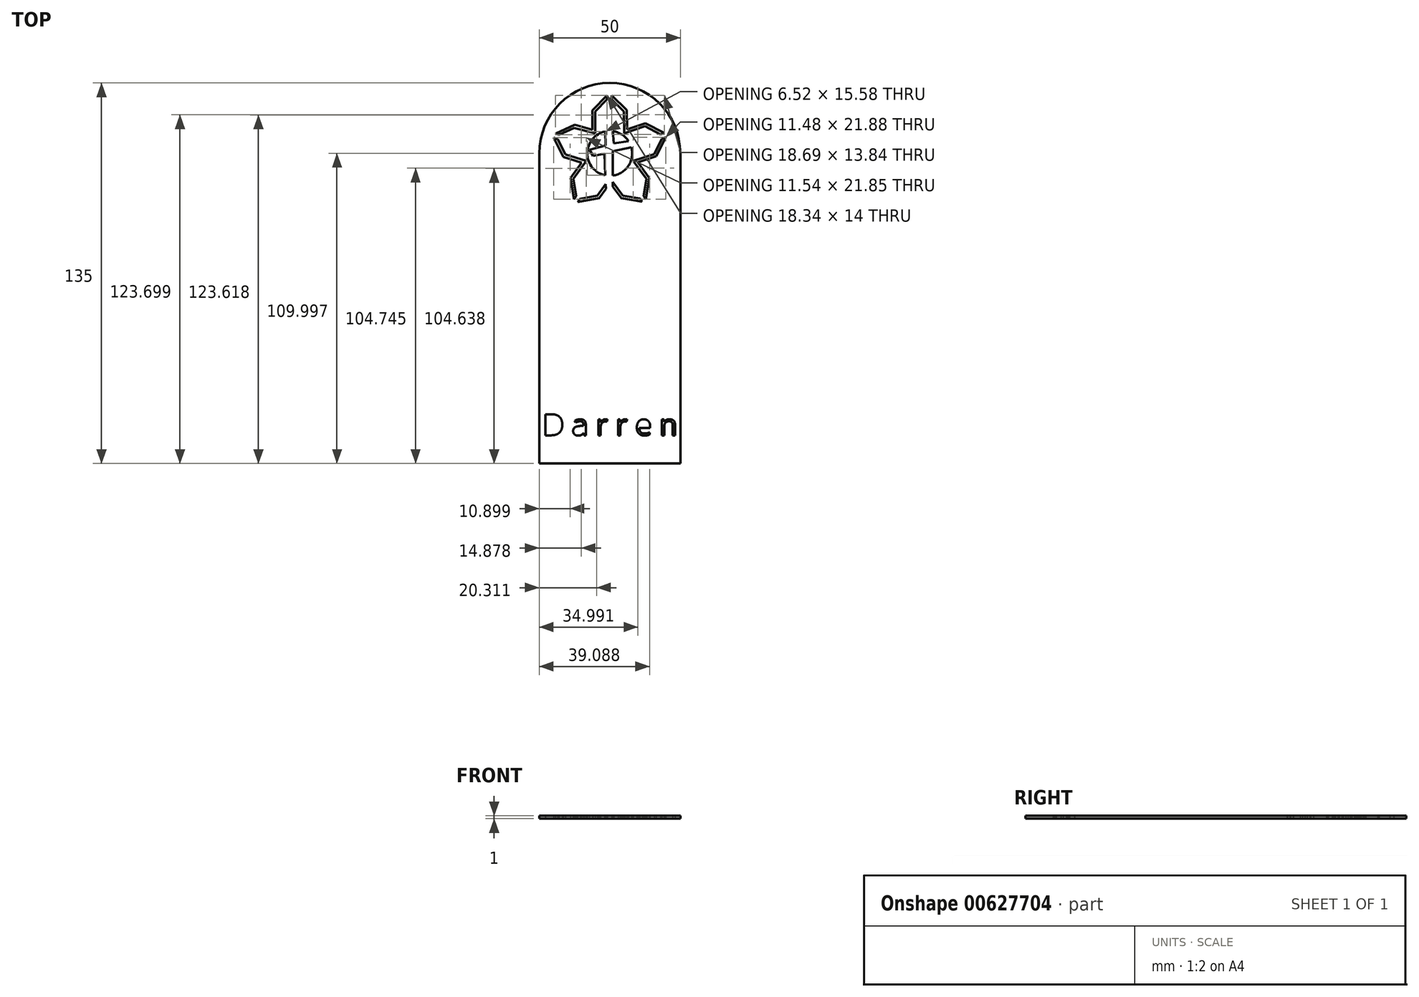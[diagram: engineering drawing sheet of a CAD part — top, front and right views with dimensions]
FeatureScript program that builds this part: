
annotation { "Feature Type Name" : "Feature", "Feature Type Description" : "" }
export const myFeature = defineFeature(function(context is Context, id is Id, definition is map)
    precondition{}
    {
        {
            var Q0;
            Q0=qCreatedBy(makeId("Top.planeOp"),FACE);
            var sketch = newSketch(context, id + "F0", { "sketchPlane" : qUnion([Q0])});
            skArc(sketch, "E0", {"start": v(1.43, 12.5) * mm, "mid": v(-23.57, 37.5) * mm, "end": v(-48.57, 12.5) * mm});
            skLineSegment(sketch, "E1", {"start": v(-28.74, 19.57) * mm, "end": v(-28.74, 27.36) * mm});
            skLineSegment(sketch, "E2", {"start": v(-28.74, 27.36) * mm, "end": v(-24.52, 31.68) * mm});
            skLineSegment(sketch, "E3", {"start": v(-22.92, 31.71) * mm, "end": v(-18.59, 27.41) * mm});
            skLineSegment(sketch, "E4", {"start": v(-18.59, 27.41) * mm, "end": v(-18.45, 19.6) * mm});
            skLineSegment(sketch, "E5", {"start": v(-18.45, 19.6) * mm, "end": v(-11.04, 22.13) * mm});
            skLineSegment(sketch, "E6", {"start": v(-11.04, 22.13) * mm, "end": v(-5.57, 19.28) * mm});
            skLineSegment(sketch, "E7", {"start": v(-5.08, 17.75) * mm, "end": v(-7.83, 12.32) * mm});
            skLineSegment(sketch, "E8", {"start": v(-7.83, 12.32) * mm, "end": v(-15.22, 9.9) * mm});
            skLineSegment(sketch, "E9", {"start": v(-15.22, 9.9) * mm, "end": v(-10.56, 3.45) * mm});
            skLineSegment(sketch, "E10", {"start": v(-10.56, 3.45) * mm, "end": v(-11.6, -2.55) * mm});
            skLineSegment(sketch, "E11", {"start": v(-12.9, -3.48) * mm, "end": v(-18.94, -2.5) * mm});
            skLineSegment(sketch, "E12", {"start": v(-18.94, -2.5) * mm, "end": v(-22.48, 2.4) * mm});
            skLineSegment(sketch, "E13", {"start": v(-27.97, -2.5) * mm, "end": v(-34.11, -3.56) * mm});
            skLineSegment(sketch, "E14", {"start": v(-35.42, -2.63) * mm, "end": v(-36.47, 3.45) * mm});
            skLineSegment(sketch, "E15", {"start": v(-36.47, 3.45) * mm, "end": v(-31.9, 9.82) * mm});
            skLineSegment(sketch, "E16", {"start": v(-31.9, 9.82) * mm, "end": v(-39.32, 12.08) * mm});
            skLineSegment(sketch, "E17", {"start": v(-39.32, 12.08) * mm, "end": v(-42.1, 17.63) * mm});
            skLineSegment(sketch, "E18", {"start": v(-41.52, 19.12) * mm, "end": v(-36.16, 21.53) * mm});
            skLineSegment(sketch, "E19", {"start": v(-36.16, 21.53) * mm, "end": v(-28.74, 19.57) * mm});
            skLineSegment(sketch, "E20", {"start": v(-22.45, 20.38) * mm, "end": v(-22.07, 16.04) * mm});
            skLineSegment(sketch, "E21", {"start": v(-22.07, 16.04) * mm, "end": v(-16.93, 16.87) * mm});
            skLineSegment(sketch, "E22", {"start": v(-15.91, 14.64) * mm, "end": v(-22.48, 13.25) * mm});
            skLineSegment(sketch, "E23", {"start": v(-22.48, 13.25) * mm, "end": v(-22.48, 4.63) * mm});
            skLineSegment(sketch, "E24", {"start": v(-24.95, -0.02) * mm, "end": v(-24.96, 0) * mm});
            skLineSegment(sketch, "E25", {"start": v(-24.96, 0) * mm, "end": v(-25.01, 1.6) * mm});
            skLineSegment(sketch, "E26", {"start": v(-25.4, 12.38) * mm, "end": v(-29.46, 11.63) * mm});
            skLineSegment(sketch, "E27", {"start": v(-29.46, 11.63) * mm, "end": v(-30.7, 13.78) * mm});
            skLineSegment(sketch, "E28", {"start": v(-30.7, 13.78) * mm, "end": v(-25, 15.25) * mm});
            skLineSegment(sketch, "E29", {"start": v(-25, 15.25) * mm, "end": v(-25.2, 20.29) * mm});
            skLineSegment(sketch, "E30", {"start": v(-48.57, 12.5) * mm, "end": v(-48.57, -97.5) * mm});
            skLineSegment(sketch, "E31", {"start": v(1.43, 12.5) * mm, "end": v(1.43, -97.5) * mm});
            skLineSegment(sketch, "E32", {"start": v(-48.57, -97.5) * mm, "end": v(1.43, -97.5) * mm});
            skLineSegment(sketch, "E33", {"start": v(-34.93, -4.7) * mm, "end": v(-27.4, -3.42) * mm});
            skLineSegment(sketch, "E34", {"start": v(-37.52, 3.69) * mm, "end": v(-36.24, -3.79) * mm});
            skLineSegment(sketch, "E35", {"start": v(-33.52, 9.27) * mm, "end": v(-37.52, 3.69) * mm});
            skLineSegment(sketch, "E36", {"start": v(-27.4, -3.42) * mm, "end": v(-24.95, -0.02) * mm});
            skLineSegment(sketch, "E37", {"start": v(-40.03, 11.25) * mm, "end": v(-33.52, 9.27) * mm});
            skLineSegment(sketch, "E38", {"start": v(-43.44, 18.06) * mm, "end": v(-40.03, 11.25) * mm});
            skLineSegment(sketch, "E39", {"start": v(-42.86, 19.56) * mm, "end": v(-35.93, 22.66) * mm});
            skLineSegment(sketch, "E40", {"start": v(-29.74, 27.76) * mm, "end": v(-29.74, 20.84) * mm});
            skLineSegment(sketch, "E41", {"start": v(-29.74, 27.76) * mm, "end": v(-24.52, 33.12) * mm});
            skLineSegment(sketch, "E42", {"start": v(-22.92, 33.12) * mm, "end": v(-17.6, 27.84) * mm});
            skLineSegment(sketch, "E43", {"start": v(-17.6, 27.84) * mm, "end": v(-17.48, 21) * mm});
            skLineSegment(sketch, "E44", {"start": v(-10.96, 23.21) * mm, "end": v(-4.23, 19.7) * mm});
            skLineSegment(sketch, "E45", {"start": v(-3.74, 18.18) * mm, "end": v(-7.12, 11.5) * mm});
            skLineSegment(sketch, "E46", {"start": v(-13.6, 9.37) * mm, "end": v(-9.5, 3.7) * mm});
            skLineSegment(sketch, "E47", {"start": v(-9.5, 3.7) * mm, "end": v(-10.78, -3.7) * mm});
            skLineSegment(sketch, "E48", {"start": v(-19.51, -3.42) * mm, "end": v(-12.09, -4.62) * mm});
            skLineSegment(sketch, "E49.trimOffspring", {"start": v(-19.51, -3.42) * mm, "end": v(-22.48, 0.7) * mm});
            skLineSegment(sketch, "E50.trimOffspring", {"start": v(-13.6, 9.37) * mm, "end": v(-7.12, 11.5) * mm});
            skLineSegment(sketch, "E51.trimOffspring", {"start": v(-35.93, 22.66) * mm, "end": v(-29.74, 20.84) * mm});
            skLineSegment(sketch, "E52.trimOffspring", {"start": v(-17.48, 21) * mm, "end": v(-10.96, 23.21) * mm});
            skLineSegment(sketch, "E53.trimOffspring", {"start": v(-25.01, 1.6) * mm, "end": v(-27.97, -2.5) * mm});
            skLineSegment(sketch, "E54.trimOffspring", {"start": v(-25.12, 4.7) * mm, "end": v(-25.4, 12.38) * mm});
            skLineSegment(sketch, "E55.trimOffspring", {"start": v(-22.48, 2.4) * mm, "end": v(-22.48, 0.7) * mm});
            skText(sketch, "E56", { "text": "D a r r e n", "fontName": "OpenSans-Regular.ttf"});
            skLineSegment(sketch, "E57", {"start": v(-36.24, -3.79) * mm, "end": v(-35.42, -2.63) * mm});
            skLineSegment(sketch, "E58", {"start": v(-34.93, -4.7) * mm, "end": v(-34.11, -3.56) * mm});
            skLineSegment(sketch, "E59", {"start": v(-12.9, -3.48) * mm, "end": v(-12.09, -4.62) * mm});
            skLineSegment(sketch, "E60", {"start": v(-11.6, -2.55) * mm, "end": v(-10.78, -3.7) * mm});
            skArc(sketch, "E61", {"start": v(-25.2, 20.29) * mm, "mid": v(-31.52, 12.47) * mm, "end": v(-25.12, 4.7) * mm});
            skArc(sketch, "E62.trimOffspring", {"start": v(-16.93, 16.87) * mm, "mid": v(-19.31, 19.22) * mm, "end": v(-22.45, 20.38) * mm});
            skArc(sketch, "E63.trimOffspring", {"start": v(-22.48, 4.63) * mm, "mid": v(-16.93, 8.14) * mm, "end": v(-15.91, 14.64) * mm});
            skLineSegment(sketch, "E64", {"start": v(-5.08, 17.75) * mm, "end": v(-3.74, 18.18) * mm});
            skLineSegment(sketch, "E65", {"start": v(-5.57, 19.28) * mm, "end": v(-4.23, 19.7) * mm});
            skLineSegment(sketch, "E66", {"start": v(-22.92, 33.12) * mm, "end": v(-22.92, 31.71) * mm});
            skLineSegment(sketch, "E67", {"start": v(-24.52, 33.12) * mm, "end": v(-24.52, 31.68) * mm});
            skLineSegment(sketch, "E68", {"start": v(-42.86, 19.56) * mm, "end": v(-41.52, 19.12) * mm});
            skLineSegment(sketch, "E69", {"start": v(-43.44, 18.06) * mm, "end": v(-42.1, 17.63) * mm});
            const initialGuessF0  = {"E56": [-0.04737, -0.0875, 1, 0, 0.00752]};
            skSetInitialGuess(sketch, initialGuessF0);
            skSolve(sketch);
        }
        {
            var Q0;
            Q0=makeQuery(id+"F0.imprint","IMPRINT",FACE,{"disambiguationData":[TD([[makeQuery(id+"F0.imprint","IMPRINT",EDGE,{"derivedFrom":sQuery(id+"F0.wireOp",EDGE,"E0")}),1.0]])]});
            extrude(context, id + "F1", {"entities" : qUnion([Q0]), "depth" : 1 * mm, "offsetDistance" : 25 * mm});
        }
    });
